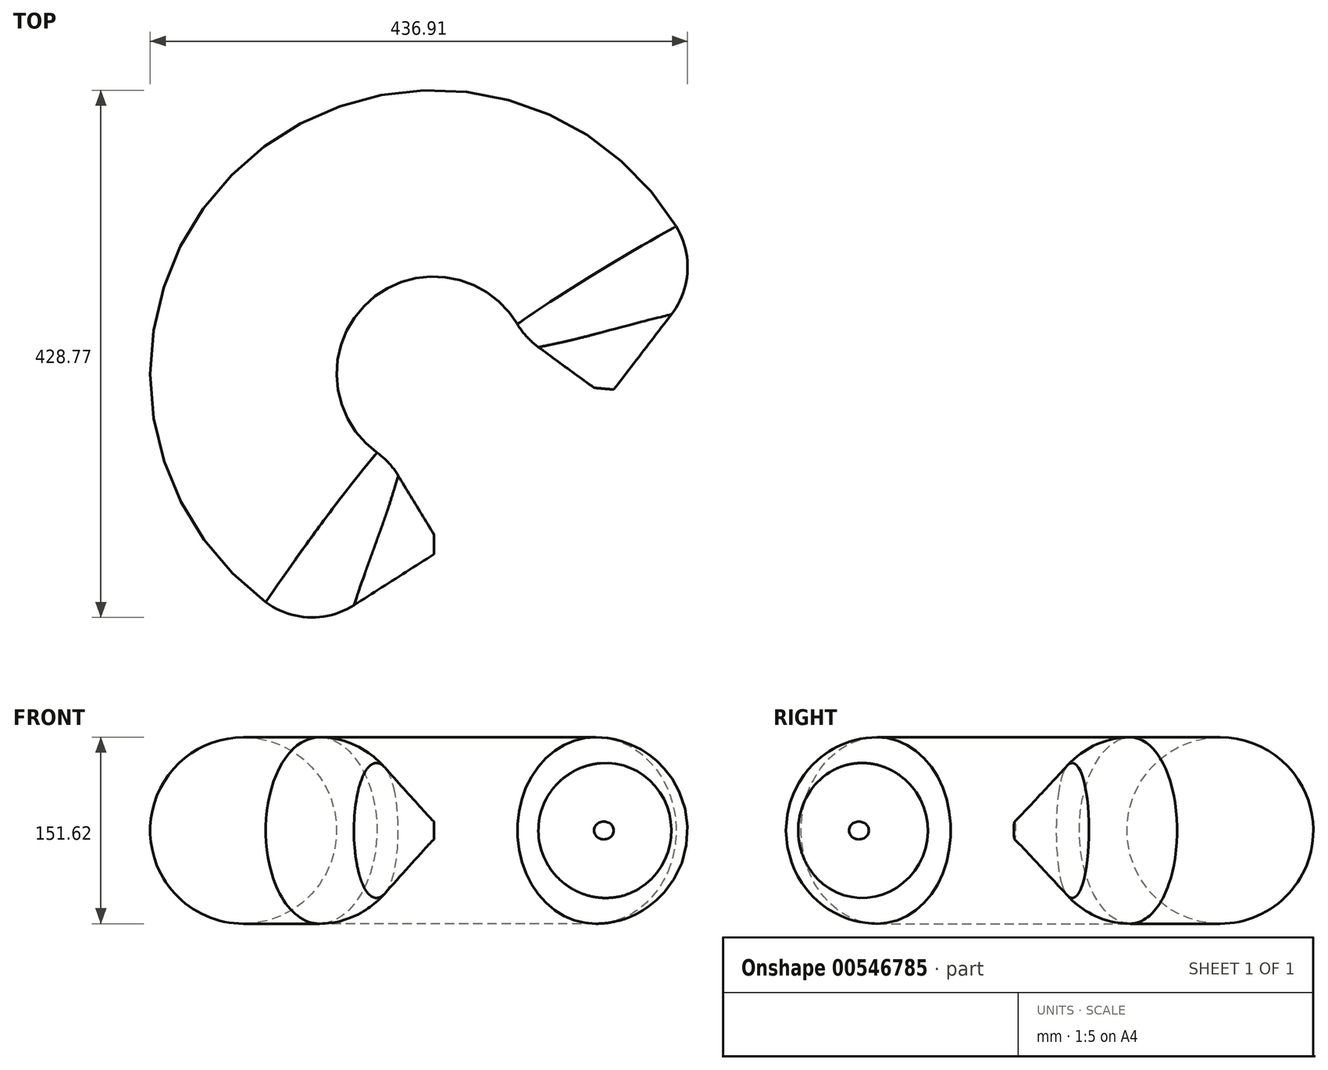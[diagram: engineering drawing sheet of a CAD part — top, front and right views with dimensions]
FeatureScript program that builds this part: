
annotation { "Feature Type Name" : "Feature", "Feature Type Description" : "" }
export const myFeature = defineFeature(function(context is Context, id is Id, definition is map)
    precondition{}
    {
        {
            var Q0;
            Q0=qCreatedBy(makeId("Right.planeOp"),FACE);
            var sketch = newSketch(context, id + "F0", { "sketchPlane" : qUnion([Q0])});
            skCircle(sketch, "E0", {"center": v(0, 0) * mm, "radius": 75.8 * mm});
            skLineSegment(sketch, "E1", {"start": v(154.84, 21.14) * mm, "end": v(154.84, -49.86) * mm});
            skSolve(sketch);
        }
        {
            var Q0;
            Q0=makeQuery(id+"F0.imprint","IMPRINT",FACE,{"disambiguationData":[TD([[makeQuery(id+"F0.imprint","IMPRINT",EDGE,{"derivedFrom":sQuery(id+"F0.wireOp",EDGE,"E0")}),1.0]])]});
            var Q1;
            Q1=sQuery(id+"F0.wireOp",EDGE,"E1");
            revolve(context, id + "F1", {"entities" : qUnion([Q0]), "axis" : qUnion([Q1]), "revolveType" : RevolveType.ONE_DIRECTION, "angle" : 275 * degree});
        }
        {
            var Q0;
            Q0=makeQuery(id+"F1.opRevolve","CAP_EDGE",EDGE,{"disambiguationData":[OSD([sQuery(id+"F0.wireOp",EDGE,"E0")])],"isStart":true});
            var Q1;
            Q1=makeQuery(id+"F1.opRevolve","CAP_EDGE",EDGE,{"disambiguationData":[OSD([sQuery(id+"F0.wireOp",EDGE,"E0")])],"isStart":false});
            chamfer(context, id + "F2", {"entities" : qUnion([Q0, Q1]), "width" : 68.58 * mm, "tangentPropagation" : true});
        }
        {
            var Q0;
            {var subQ0=sQuery(id+"F0.wireOp",EDGE,"E0");Q0=makeQuery(id+"F2.opChamfer","BLEND_EDGE",EDGE,{"blendedFrom":[makeQuery(id+"F1.opRevolve","CAP_EDGE",EDGE,{"disambiguationData":[OSD([subQ0])],"isStart":true}),makeQuery(id+"F1.opRevolve","SWEPT_FACE",FACE,{"disambiguationData":[OSD([subQ0])]})],"blendedInto":[makeQuery(id+"F1.opRevolve","SWEPT_FACE",FACE,{"disambiguationData":[OSD([subQ0])]})]});}
            var Q1;
            {var subQ0=sQuery(id+"F0.wireOp",EDGE,"E0");Q1=makeQuery(id+"F2.opChamfer","BLEND_EDGE",EDGE,{"blendedFrom":[makeQuery(id+"F1.opRevolve","CAP_EDGE",EDGE,{"disambiguationData":[OSD([subQ0])],"isStart":false}),makeQuery(id+"F1.opRevolve","SWEPT_FACE",FACE,{"disambiguationData":[OSD([subQ0])]})],"blendedInto":[makeQuery(id+"F1.opRevolve","SWEPT_FACE",FACE,{"disambiguationData":[OSD([subQ0])]})]});}
            fillet(context, id + "F3", {"entities" : qUnion([Q0, Q1]), "radius" : 63.5 * mm, "tangentPropagation" : true, "allowEdgeOverflow" : false});
        }
    });
